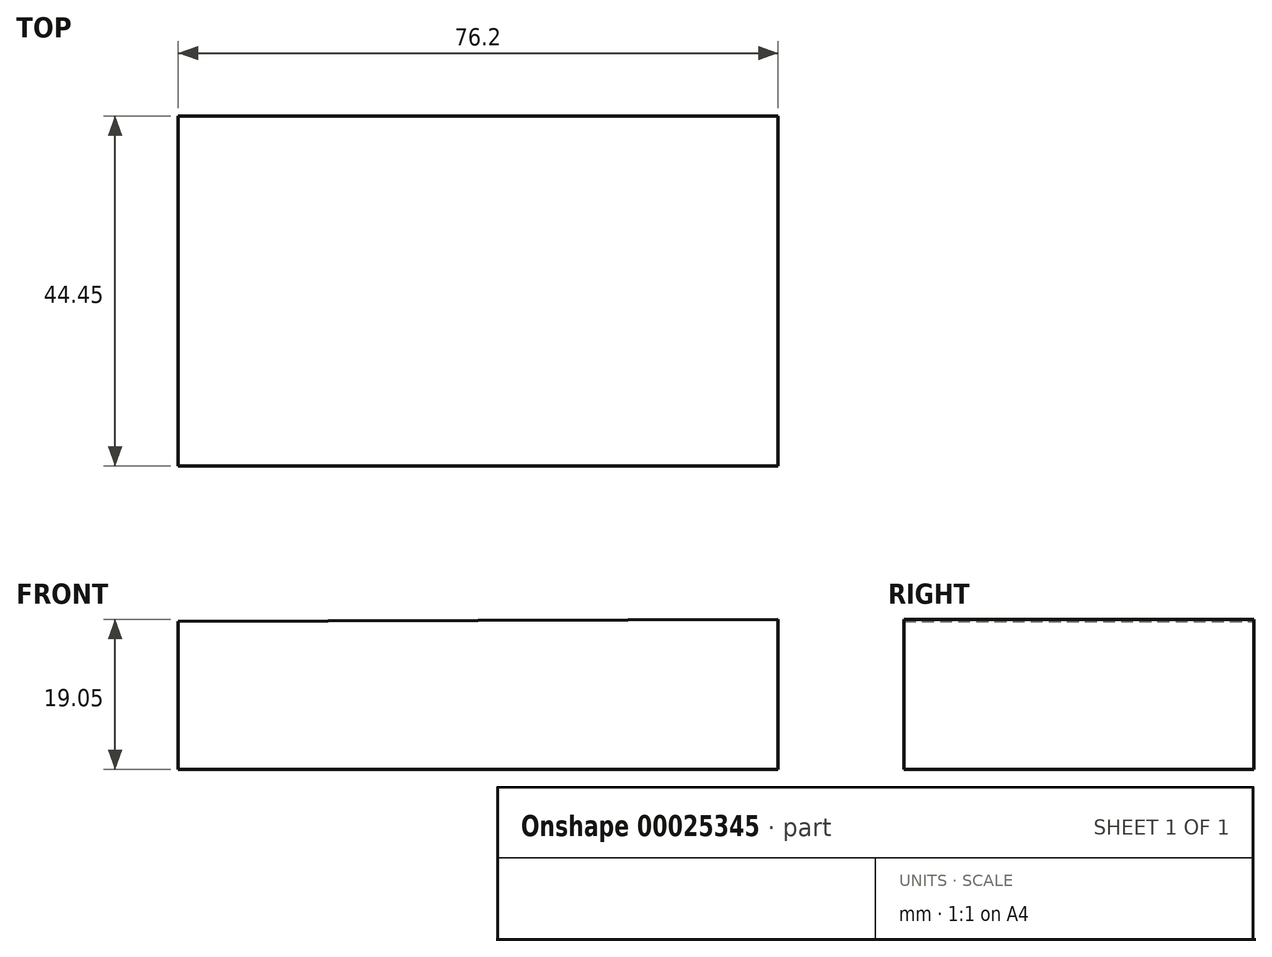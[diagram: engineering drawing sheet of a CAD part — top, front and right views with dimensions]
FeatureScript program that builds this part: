
annotation { "Feature Type Name" : "Feature", "Feature Type Description" : "" }
export const myFeature = defineFeature(function(context is Context, id is Id, definition is map)
    precondition{}
    {
        {
            var Q0;
            Q0=qCreatedBy(makeId("Front.planeOp"),FACE);
            var sketch = newSketch(context, id + "F0", { "sketchPlane" : qUnion([Q0])});
            skLineSegment(sketch, "E0", {"start": v(-43.73, 34.63) * mm, "end": v(-43.73, 15.84) * mm});
            skLineSegment(sketch, "E1", {"start": v(-43.73, 15.84) * mm, "end": v(32.47, 15.84) * mm});
            skLineSegment(sketch, "E2", {"start": v(32.47, 15.84) * mm, "end": v(32.47, 34.89) * mm});
            skLineSegment(sketch, "E3", {"start": v(-43.73, 34.63) * mm, "end": v(32.47, 34.89) * mm});
            skSolve(sketch);
        }
        {
            var Q0;
            Q0 = qSketchRegion(id + "F0", true);
            extrude(context, id + "F1", {"entities" : qUnion([Q0]), "depth" : 44.45 * mm});
        }
    });
